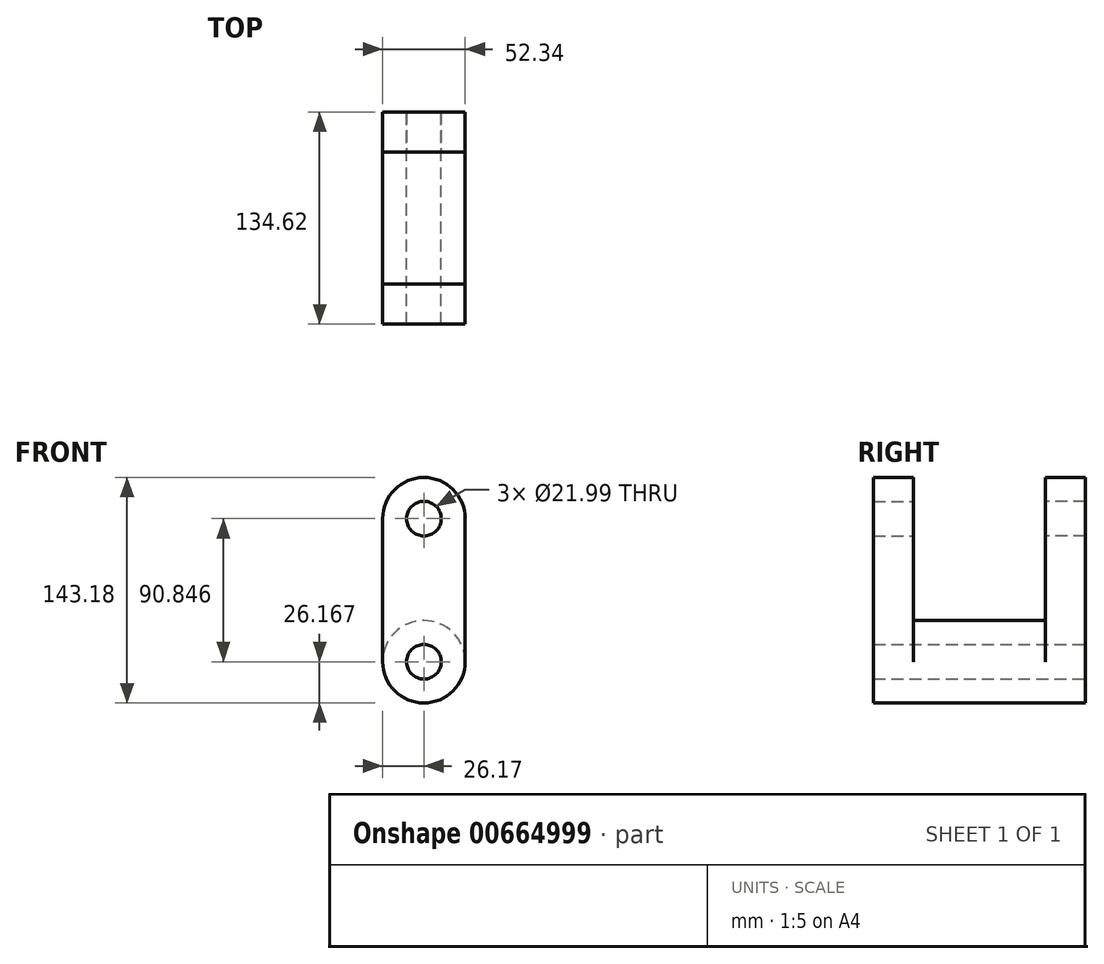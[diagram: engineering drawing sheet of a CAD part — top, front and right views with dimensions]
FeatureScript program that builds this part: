
annotation { "Feature Type Name" : "Feature", "Feature Type Description" : "" }
export const myFeature = defineFeature(function(context is Context, id is Id, definition is map)
    precondition{}
    {
        {
            var Q0;
            Q0=qCreatedBy(makeId("Front.planeOp"),FACE);
            var sketch = newSketch(context, id + "F0", { "sketchPlane" : qUnion([Q0])});
            skLineSegment(sketch, "E0.left", {"start": v(-26.17, 45.42) * mm, "end": v(-26.17, -45.42) * mm});
            skLineSegment(sketch, "E0.right", {"start": v(26.17, 45.42) * mm, "end": v(26.17, -45.42) * mm});
            skPoint(sketch, "E0.middle", {"position": v(0, 0) * mm});
            skArc(sketch, "E1", {"start": v(26.17, 45.42) * mm, "mid": v(0, 71.59) * mm, "end": v(-26.17, 45.42) * mm});
            skCircle(sketch, "E2", {"center": v(0, -45.42) * mm, "radius": 11 * mm});
            skCircle(sketch, "E3", {"center": v(0, 45.42) * mm, "radius": 11 * mm});
            skArc(sketch, "E4", {"start": v(-26.17, -45.42) * mm, "mid": v(0, -71.59) * mm, "end": v(26.17, -45.42) * mm});
            skArc(sketch, "E5", {"start": v(26.17, -45.42) * mm, "mid": v(0, -19.26) * mm, "end": v(-26.17, -45.42) * mm});
            skSolve(sketch);
        }
        {
            var Q0;
            Q0 = qSketchRegion(id + "F0", true);
            extrude(context, id + "F1", {"entities" : qUnion([Q0]), "depth" : 25.4 * mm, "offsetDistance" : 25.4 * mm});
        }
        {
            var Q0;
            Q0=makeQuery(id+"F0.imprint","IMPRINT",FACE,{"disambiguationData":[TD([[makeQuery(id+"F0.imprint","IMPRINT",EDGE,{"derivedFrom":sQuery(id+"F0.wireOp",EDGE,"E2")}),-1.0]])]});
            extrude(context, id + "F2", {"entities" : qUnion([Q0]), "operationType" : NewBodyOperationType.ADD, "oppositeDirection" : true, "depth" : 41.9 * mm, "offsetDistance" : 25.4 * mm});
        }
        {
            var Q0;
            Q0=makeQuery(id+"F1.opExtrude","SWEPT_BODY",BODY,{"disambiguationData":[OSD([sQuery(id+"F0.wireOp",EDGE,"E0.left"),sQuery(id+"F0.wireOp",EDGE,"E0.right"),sQuery(id+"F0.wireOp",EDGE,"E1"),sQuery(id+"F0.wireOp",EDGE,"E2"),sQuery(id+"F0.wireOp",EDGE,"E3"),sQuery(id+"F0.wireOp",EDGE,"E4")])]});
            var Q1;
            Q1=makeQuery(id+"F2.opExtrude","CAP_FACE",FACE,{"disambiguationData":[OSD([sQuery(id+"F0.wireOp",EDGE,"E2"),sQuery(id+"F0.wireOp",EDGE,"E4"),sQuery(id+"F0.wireOp",EDGE,"E5")])],"isStart":false});
            mirror(context, id + "F3", {"operationType" : NewBodyOperationType.ADD, "entities" : qUnion([Q0]), "mirrorPlane" : qUnion([Q1])});
        }
    });
